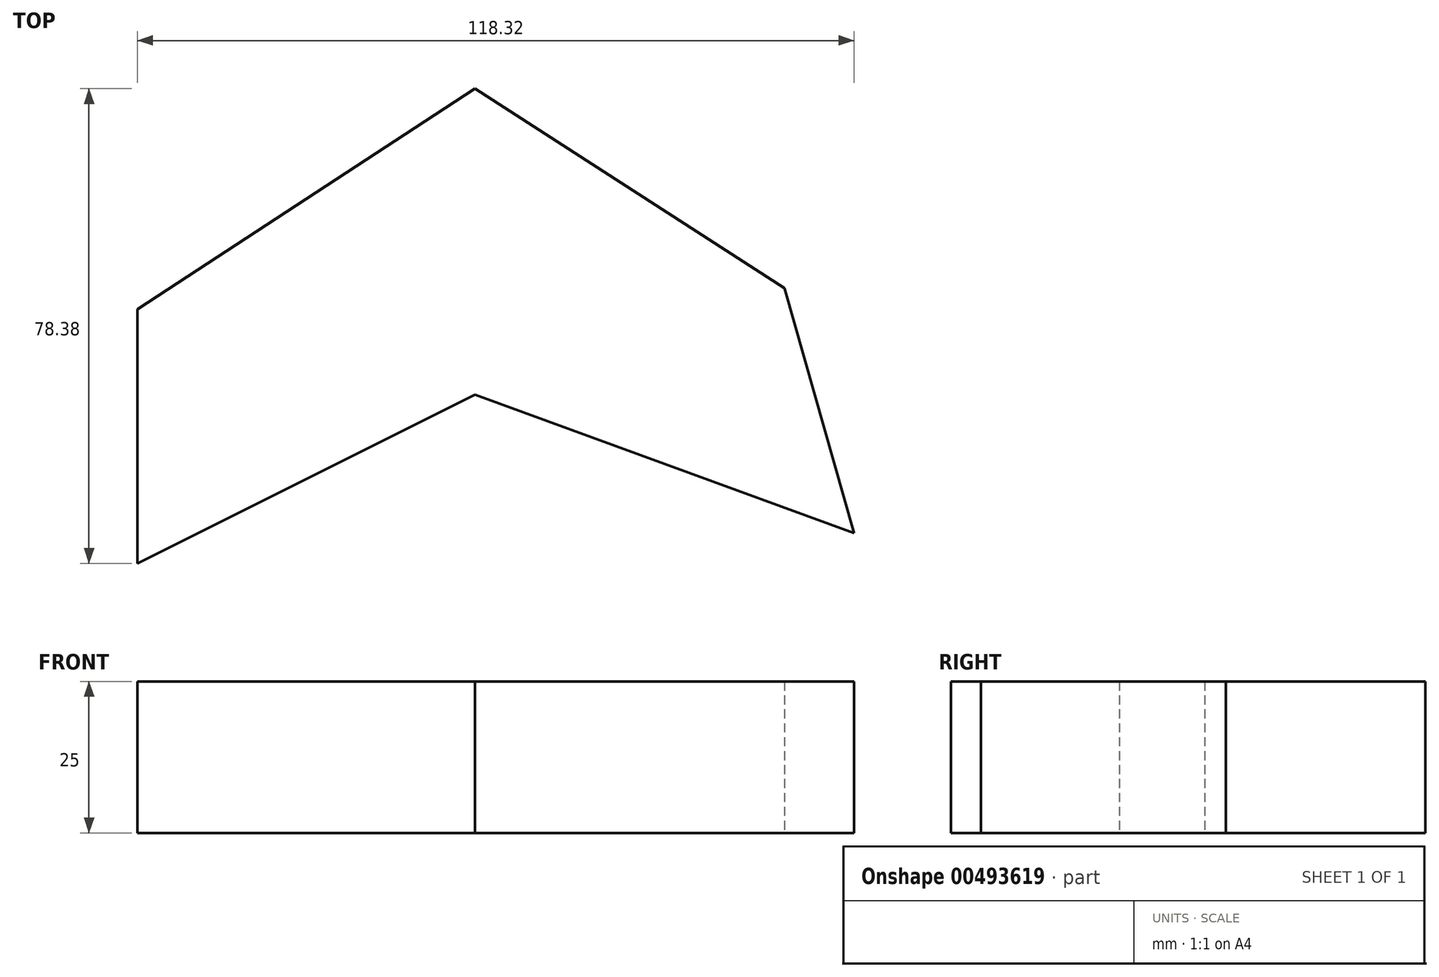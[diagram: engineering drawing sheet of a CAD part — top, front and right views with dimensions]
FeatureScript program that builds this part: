
annotation { "Feature Type Name" : "Feature", "Feature Type Description" : "" }
export const myFeature = defineFeature(function(context is Context, id is Id, definition is map)
    precondition{}
    {
        {
            var Q0;
            Q0=qCreatedBy(makeId("Top.planeOp"),FACE);
            var sketch = newSketch(context, id + "F0", { "sketchPlane" : qUnion([Q0])});
            skLineSegment(sketch, "E0", {"start": v(-55.7, -27.86) * mm, "end": v(-55.7, 14.07) * mm});
            skLineSegment(sketch, "E1", {"start": v(-55.7, 14.07) * mm, "end": v(0, 50.52) * mm});
            skLineSegment(sketch, "E2", {"start": v(0, 50.52) * mm, "end": v(51.14, 17.57) * mm});
            skLineSegment(sketch, "E3", {"start": v(51.14, 17.57) * mm, "end": v(62.62, -22.87) * mm});
            skLineSegment(sketch, "E4", {"start": v(62.62, -22.87) * mm, "end": v(0, 0) * mm});
            skLineSegment(sketch, "E5", {"start": v(0, 0) * mm, "end": v(-55.7, -27.86) * mm});
            skSolve(sketch);
        }
        {
            var Q0;
            Q0=makeQuery(id+"F0.imprint","IMPRINT",FACE,{"disambiguationData":[TD([[makeQuery(id+"F0.imprint","IMPRINT",EDGE,{"derivedFrom":sQuery(id+"F0.wireOp",EDGE,"E0")}),-1.0]])]});
            extrude(context, id + "F1", {"entities" : qUnion([Q0]), "depth" : 25 * mm});
        }
    });
